# Revit family: Lavatory-Zurn-Z5003
name_source: partatom
category: Plumbing Fixtures
units: mm (PartAtom-declared; Revit-internal decimal feet)

## family parameters
Cut with Voids When Loaded = No
Host = Face
Maintain Annotation Orientation = No
OmniClass Number = 23.45.00.00
OmniClass Title = Sanitary, Laundry, and Cleaning Equipment
Part Type = Normal
Room Calculation Point = No
Round Connector Dimension = Use Diameter
Shared = No

## types (3) — shared parameters
Assembly Code = D2010.60
CW Connection = No
Default Elevation = 48 "
HW Connection = No
Height of (SINK+ SHROUD) = 25.5 "
Manufacturer = Zurn Water, LLC
Manufacturer Brand = Zurn
Mode of Installation = Wall Mounted
Modified Date = 07/09/2025
Product Documentation Link = https://files.zurn.com
Product Installation Sheet URL = https://files.zurn.com
Product Page URL = https://www.zurn.com
Product data URL = https://bimobject.com
Shroud Material = Stainless Steel_ Zurn_ Finish
Sink Material = Porcelain-Zurn-White
URL = https://www.zurn.com
Vent Connection = No
Waste Connection = Yes
zero-valued in all types: CWFU, HWFU, WFU

## per-type parameters (varying)
| type | Description | Double Shroud Assembly | Model | Single Shroud Assembly | Triple Shroud Assembly | Width of the Sink |
| Z5003.01 (Sundara® Drift Single Basin Hand Washing System) | Sundara® Drift Single Basin Hand Washing System | No | Z5003.01 | Yes | No | 30 " |
| Z5003.02 (Sundara® Drift Double Basin Hand Washing System) | Sundara® Drift Double Basin Hand Washing System | Yes | Z5003.02 | No | No | 60 " |
| Z5003.03 (Sundara® Drift Triple Basin Hand Washing System) | Sundara® Drift Triple Basin Hand Washing System | No | Z5003.03 | No | Yes | 90 " |

## geometry (parser evidence)
native form markers: Sweep x9
no freeform markers — native parametric forms only
